# Revit family: sh-236J
name_source: partatom
category: Lighting Fixtures
revit_build: Autodesk Revit 2017 (Build: 20160225_1515(x64)
units: mm (PartAtom-declared; Revit-internal decimal feet)

## family parameters
Cut with Voids When Loaded = No
Host = Face
Light Source = Yes
Part Type = Normal
Room Calculation Point = No
Round Connector Dimension = Use Diameter
Shared = No

## types (1)
- SH-236J(polycarbonate body-led lamp-T8)
    Body Material = polycarbonate
    Color Filter = 16777215
    Default Elevation = 121.9 cm
    Dimming Lamp Color Temperature Shift = <None>
    Emit from Line Length = 61.0 cm
    Height = 9.0 cm
    IP = IP65
    Lamp = LED
    Length = 65.9 cm
    Manufacturer = SHOA
    Model = SH-236J
    Number of Lamps = 2
    Photometric Web File = FLOODLIGHT_LED_5730_100W_CW.IES
    Protection Class = Class II
    Tilt Angle = 90.00°
    Voltage/Frequency = 230V-50HZ
    Website = www.shoaco.com
    Width = 12.9 cm
    color rendering index(CRI) = 80
    color temperature = 4000K
    consumption current = 0 A
    instalation = Surface Mounted
    wattage. = 36 W

## geometry (parser evidence)
native form markers: Sweep x3
no freeform markers — native parametric forms only
